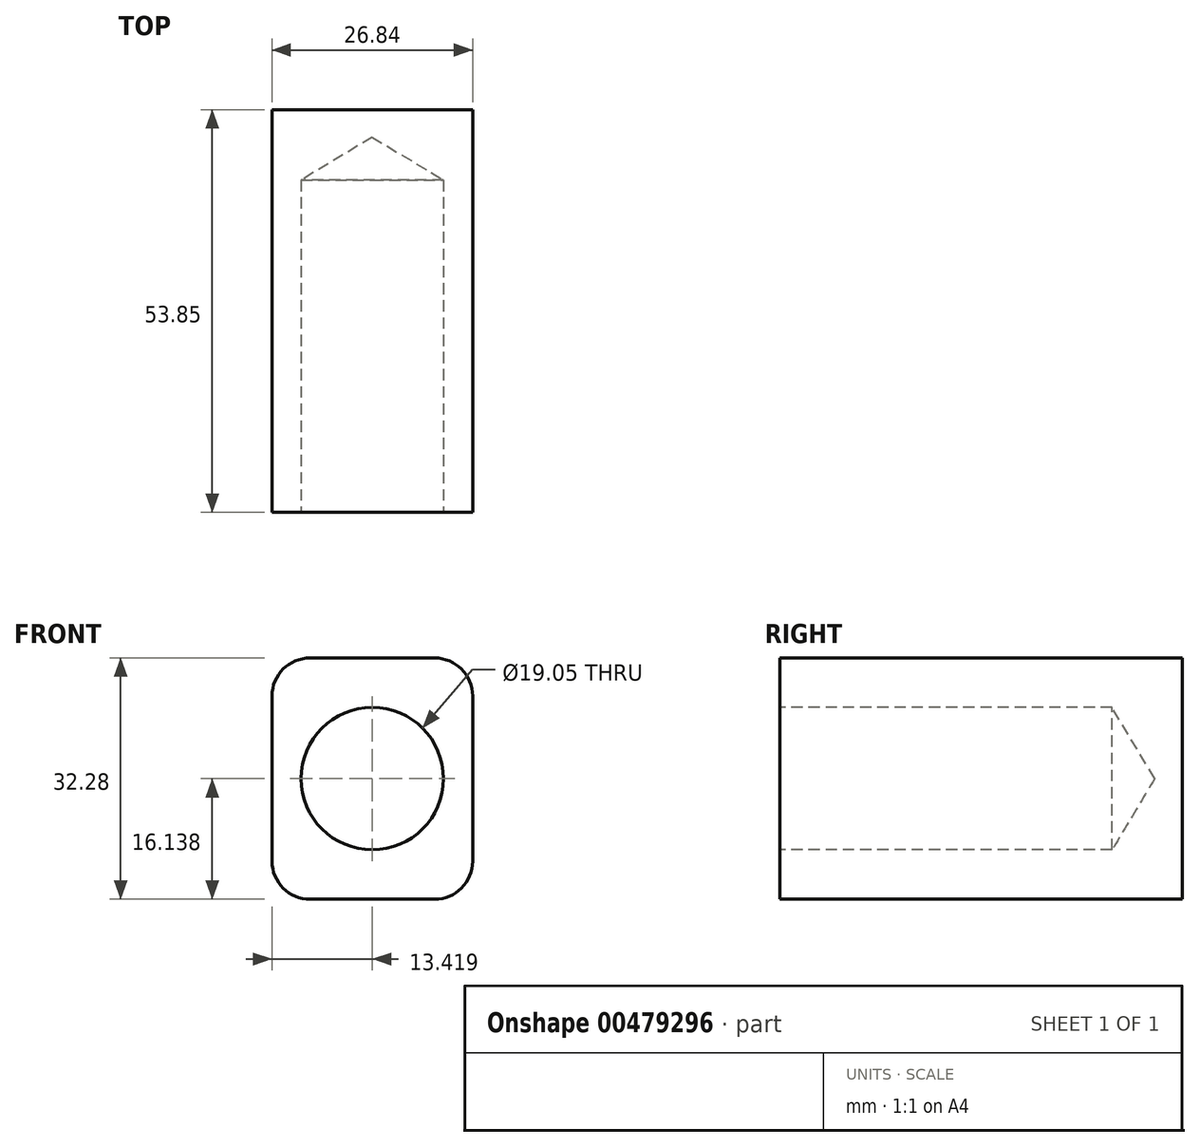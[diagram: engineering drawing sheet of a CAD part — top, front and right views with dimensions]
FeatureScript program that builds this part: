
annotation { "Feature Type Name" : "Feature", "Feature Type Description" : "" }
export const myFeature = defineFeature(function(context is Context, id is Id, definition is map)
    precondition{}
    {
        {
            var Q0;
            Q0=qCreatedBy(makeId("Front.planeOp"),FACE);
            var sketch = newSketch(context, id + "F0", { "sketchPlane" : qUnion([Q0])});
            skLineSegment(sketch, "E0.bottom", {"start": v(0, 0) * mm, "end": v(26.84, 0) * mm});
            skLineSegment(sketch, "E0.top", {"start": v(0, 32.28) * mm, "end": v(26.84, 32.28) * mm});
            skLineSegment(sketch, "E0.left", {"start": v(0, 0) * mm, "end": v(0, 32.28) * mm});
            skLineSegment(sketch, "E0.right", {"start": v(26.84, 0) * mm, "end": v(26.84, 32.28) * mm});
            skSolve(sketch);
        }
        {
            var Q0;
            Q0=makeQuery(id+"F0.imprint","IMPRINT",FACE,{"disambiguationData":[TD([[makeQuery(id+"F0.imprint","IMPRINT",EDGE,{"derivedFrom":sQuery(id+"F0.wireOp",EDGE,"E0.bottom")}),1.0]])]});
            extrude(context, id + "F1", {"entities" : qUnion([Q0]), "depth" : 53.85 * mm});
        }
        {
            var Q0;
            Q0=makeQuery(id+"F1.opExtrude","CAP_FACE",FACE,{"disambiguationData":[OSD([sQuery(id+"F0.wireOp",EDGE,"E0.bottom"),sQuery(id+"F0.wireOp",EDGE,"E0.top"),sQuery(id+"F0.wireOp",EDGE,"E0.left"),sQuery(id+"F0.wireOp",EDGE,"E0.right")])],"isStart":false});
            var sketch = newSketch(context, id + "F2", { "sketchPlane" : qUnion([Q0])});
            skCircle(sketch, "E1", {"center": v(11.9, 14.5) * mm, "radius": 10.45 * mm});
            skSolve(sketch);
        }
        {
            var Q0;
            Q0=makeQuery(id+"F2.imprint","IMPRINT",FACE,{"disambiguationData":[TD([[makeQuery(id+"F2.imprint","IMPRINT",EDGE,{"derivedFrom":sQuery(id+"F2.wireOp",EDGE,"E1")}),1.0]])]});
            extrude(context, id + "F3", {"entities" : qUnion([Q0]), "operationType" : NewBodyOperationType.ADD, "oppositeDirection" : true, "depth" : 43.69 * mm});
        }
        {
            var Q0;
            Q0=makeQuery(id+"F1.opExtrude","CAP_FACE",FACE,{"disambiguationData":[OSD([sQuery(id+"F0.wireOp",EDGE,"E0.bottom"),sQuery(id+"F0.wireOp",EDGE,"E0.top"),sQuery(id+"F0.wireOp",EDGE,"E0.left"),sQuery(id+"F0.wireOp",EDGE,"E0.right")])],"isStart":false});
            var sketch = newSketch(context, id + "F4", { "sketchPlane" : qUnion([Q0])});
            skCircle(sketch, "E2", {"center": v(13.18, 16) * mm, "radius": 11.74 * mm});
            skSolve(sketch);
        }
        {
            var Q0;
            Q0=sQuery(id+"F4.wireOp",EDGE,"E2");
            extrude(context, id + "F5", {"bodyType" : ToolBodyType.SURFACE, "surfaceEntities" : qUnion([Q0]), "oppositeDirection" : true, "depth" : 36.83 * mm});
        }
        {
            var Q0;
            Q0=makeQuery(id+"F1.opExtrude","CAP_FACE",FACE,{"disambiguationData":[OSD([sQuery(id+"F0.wireOp",EDGE,"E0.bottom"),sQuery(id+"F0.wireOp",EDGE,"E0.top"),sQuery(id+"F0.wireOp",EDGE,"E0.left"),sQuery(id+"F0.wireOp",EDGE,"E0.right")])],"isStart":false});
            var sketch = newSketch(context, id + "F6", { "sketchPlane" : qUnion([Q0])});
            skPoint(sketch, "E3", {"position": v(13.42, 16.14) * mm});
            skPoint(sketch, "E3.positionSnap0", {"position": v(13.42, 32.28) * mm});
            skPoint(sketch, "E3.positionSnap1", {"position": v(26.84, 16.14) * mm});
            skSolve(sketch);
        }
        {
            var Q0;
            Q0=sQuery(id+"F6.wireOp",VERTEX,"E3");
            var Q1;
            Q1=makeQuery(id+"F1.opExtrude","SWEPT_BODY",BODY,{"disambiguationData":[OSD([sQuery(id+"F0.wireOp",EDGE,"E0.bottom"),sQuery(id+"F0.wireOp",EDGE,"E0.top"),sQuery(id+"F0.wireOp",EDGE,"E0.left"),sQuery(id+"F0.wireOp",EDGE,"E0.right")])]});
            hole(context, id + "F7", {"style" : HoleStyle.SIMPLE, "endStyle" : HoleEndStyle.BLIND, "holeDiameter" : 19.05 * mm, "holeDepth" : 44.45 * mm, "isTappedThrough" : true, "tappedDepth" : 12.7 * mm, "tapClearance" : 3, "locations" : qUnion([Q0]), "scope" : qUnion([Q1])});
        }
        {
            var Q0;
            Q0=makeQuery(id+"F1.opExtrude","SWEPT_EDGE",EDGE,{"disambiguationData":[OSD([sQuery(id+"F0.wireOp",EDGE,"E0.top"),sQuery(id+"F0.wireOp",EDGE,"E0.left")])]});
            var Q1;
            Q1=makeQuery(id+"F1.opExtrude","SWEPT_EDGE",EDGE,{"disambiguationData":[OSD([sQuery(id+"F0.wireOp",EDGE,"E0.top"),sQuery(id+"F0.wireOp",EDGE,"E0.right")])]});
            var Q2;
            Q2=makeQuery(id+"F1.opExtrude","SWEPT_EDGE",EDGE,{"disambiguationData":[OSD([sQuery(id+"F0.wireOp",EDGE,"E0.bottom"),sQuery(id+"F0.wireOp",EDGE,"E0.right")])]});
            var Q3;
            Q3=makeQuery(id+"F1.opExtrude","SWEPT_EDGE",EDGE,{"disambiguationData":[OSD([sQuery(id+"F0.wireOp",EDGE,"E0.bottom"),sQuery(id+"F0.wireOp",EDGE,"E0.left")])]});
            fillet(context, id + "F8", {"entities" : qUnion([Q0, Q1, Q2, Q3]), "radius" : 5.08 * mm, "tangentPropagation" : true, "allowEdgeOverflow" : false});
        }
    });
